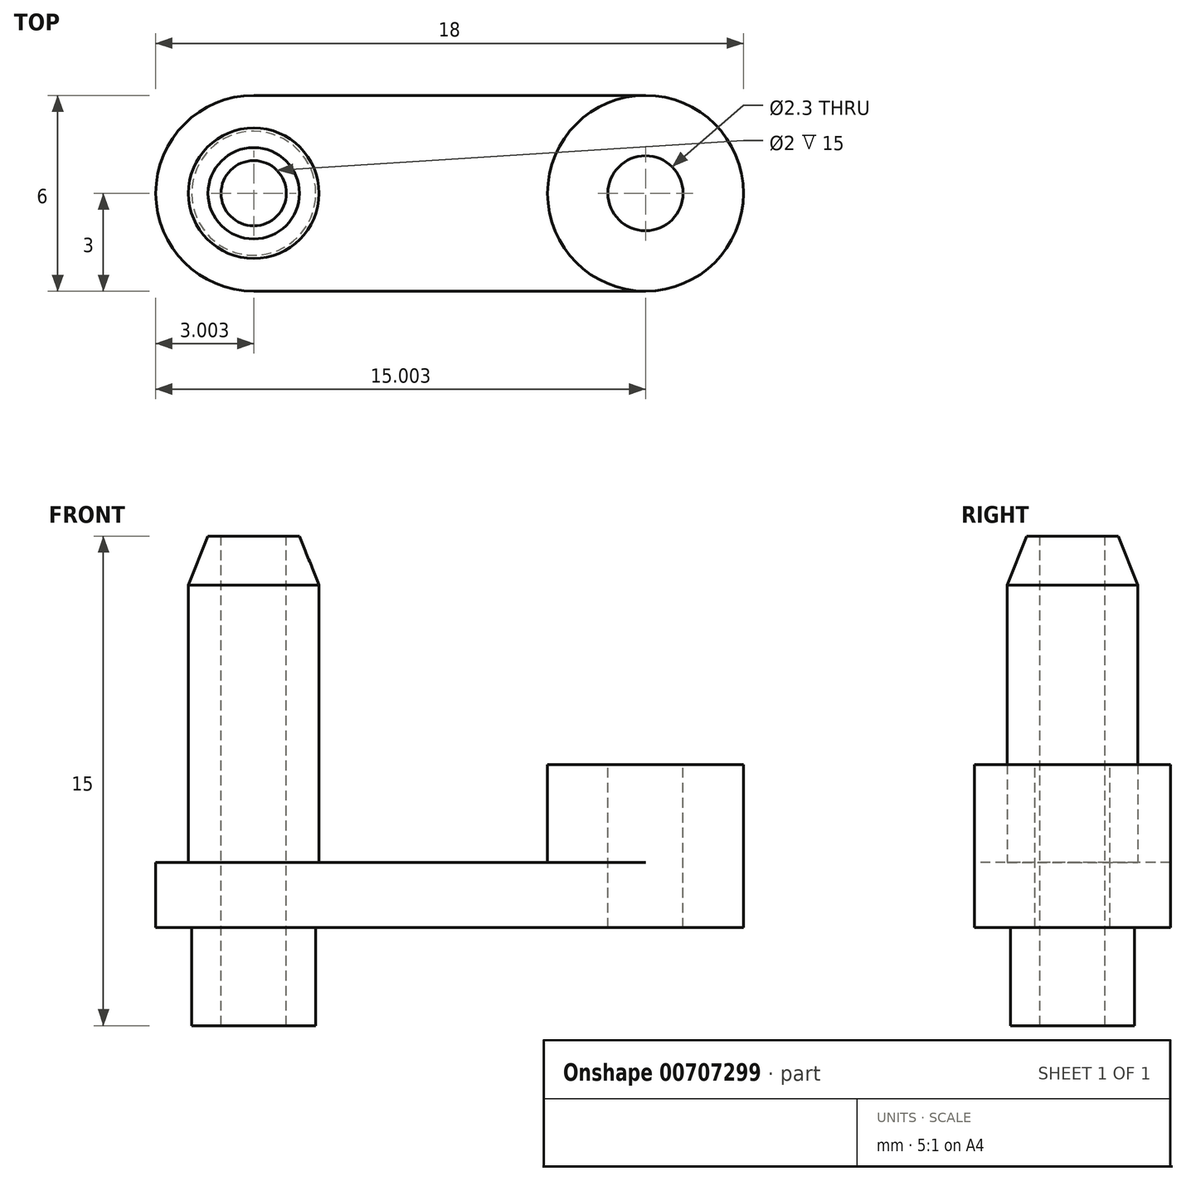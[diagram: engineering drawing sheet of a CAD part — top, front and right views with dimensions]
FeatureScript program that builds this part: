
annotation { "Feature Type Name" : "Feature", "Feature Type Description" : "" }
export const myFeature = defineFeature(function(context is Context, id is Id, definition is map)
    precondition{}
    {
        {
            var Q0;
            Q0=qCreatedBy(makeId("Top.planeOp"),FACE);
            var sketch = newSketch(context, id + "F0", { "sketchPlane" : qUnion([Q0])});
            skLineSegment(sketch, "E0.bottom", {"start": v(-7.1, 3) * mm, "end": v(10.9, 3) * mm});
            skLineSegment(sketch, "E0.top", {"start": v(-7.1, -3) * mm, "end": v(10.9, -3) * mm});
            skLineSegment(sketch, "E0.left", {"start": v(-7.1, 3) * mm, "end": v(-7.1, -3) * mm});
            skLineSegment(sketch, "E0.right", {"start": v(10.9, 3) * mm, "end": v(10.9, -3) * mm});
            skSolve(sketch);
        }
        {
            var Q0;
            Q0 = qSketchRegion(id + "F0", true);
            extrude(context, id + "F1", {"entities" : qUnion([Q0]), "depth" : 2 * mm, "offsetDistance" : 25 * mm});
        }
        {
            var Q0;
            Q0=makeQuery(id+"F1.opExtrude","CAP_FACE",FACE,{"disambiguationData":[OSD([sQuery(id+"F0.wireOp",EDGE,"E0.bottom"),sQuery(id+"F0.wireOp",EDGE,"E0.top"),sQuery(id+"F0.wireOp",EDGE,"E0.left"),sQuery(id+"F0.wireOp",EDGE,"E0.right")])],"isStart":false});
            var sketch = newSketch(context, id + "F2", { "sketchPlane" : qUnion([Q0])});
            skCircle(sketch, "E1", {"center": v(7.9, 0) * mm, "radius": 3 * mm});
            skCircle(sketch, "E2", {"center": v(-4.1, 0) * mm, "radius": 2 * mm});
            skSolve(sketch);
        }
        {
            var Q0;
            Q0 = qSketchRegion(id + "F2", true);
            extrude(context, id + "F3", {"entities" : qUnion([Q0]), "operationType" : NewBodyOperationType.ADD, "depth" : 10 * mm, "offsetDistance" : 25 * mm});
        }
        {
            var Q0;
            Q0=makeQuery(id+"F3.opExtrude","CAP_FACE",FACE,{"disambiguationData":[OSD([sQuery(id+"F2.wireOp",EDGE,"E2")])],"isStart":false});
            var sketch = newSketch(context, id + "F4", { "sketchPlane" : qUnion([Q0])});
            skCircle(sketch, "E3", {"center": v(-4.1, 0) * mm, "radius": 1 * mm});
            skCircle(sketch, "E4", {"center": v(7.9, 0) * mm, "radius": 1.15 * mm});
            skSolve(sketch);
        }
        {
            var Q0;
            Q0 = qSketchRegion(id + "F4", true);
            extrude(context, id + "F5", {"entities" : qUnion([Q0]), "operationType" : NewBodyOperationType.REMOVE, "oppositeDirection" : true, "depth" : 20 * mm, "offsetDistance" : 25 * mm});
        }
        {
            var Q0;
            Q0=makeQuery(id+"F3.opExtrude","CAP_EDGE",EDGE,{"disambiguationData":[OSD([sQuery(id+"F2.wireOp",EDGE,"E2")])],"isStart":false});
            chamfer(context, id + "F6", {"entities" : qUnion([Q0]), "chamferType" : ChamferType.TWO_OFFSETS, "width1" : 0.6 * mm, "oppositeDirection" : false, "width2" : 1.5 * mm, "tangentPropagation" : true});
        }
        {
            var Q0;
            Q0=makeQuery(id+"F3.opExtrude","CAP_FACE",FACE,{"disambiguationData":[OSD([sQuery(id+"F2.wireOp",EDGE,"E1")])],"isStart":false});
            var sketch = newSketch(context, id + "F7", { "sketchPlane" : qUnion([Q0])});
            skLineSegment(sketch, "E5.bottom", {"start": v(1.79, 5.38) * mm, "end": v(13.39, 5.38) * mm});
            skLineSegment(sketch, "E5.top", {"start": v(1.79, -6.45) * mm, "end": v(13.39, -6.45) * mm});
            skLineSegment(sketch, "E5.left", {"start": v(1.79, 5.38) * mm, "end": v(1.79, -6.45) * mm});
            skLineSegment(sketch, "E5.right", {"start": v(13.39, 5.38) * mm, "end": v(13.39, -6.45) * mm});
            skSolve(sketch);
        }
        {
            var Q0;
            Q0 = qSketchRegion(id + "F7", true);
            extrude(context, id + "F8", {"entities" : qUnion([Q0]), "operationType" : NewBodyOperationType.REMOVE, "oppositeDirection" : true, "depth" : 7 * mm, "offsetDistance" : 25 * mm});
        }
        {
            var Q0;
            Q0=makeQuery(id+"F1.opExtrude","SWEPT_EDGE",EDGE,{"disambiguationData":[OSD([sQuery(id+"F0.wireOp",EDGE,"E0.top"),sQuery(id+"F0.wireOp",EDGE,"E0.right")])]});
            var Q1;
            Q1=makeQuery(id+"F1.opExtrude","SWEPT_EDGE",EDGE,{"disambiguationData":[OSD([sQuery(id+"F0.wireOp",EDGE,"E0.bottom"),sQuery(id+"F0.wireOp",EDGE,"E0.right")])]});
            var Q2;
            Q2=makeQuery(id+"F1.opExtrude","SWEPT_EDGE",EDGE,{"disambiguationData":[OSD([sQuery(id+"F0.wireOp",EDGE,"E0.bottom"),sQuery(id+"F0.wireOp",EDGE,"E0.left")])]});
            var Q3;
            Q3=makeQuery(id+"F1.opExtrude","SWEPT_EDGE",EDGE,{"disambiguationData":[OSD([sQuery(id+"F0.wireOp",EDGE,"E0.top"),sQuery(id+"F0.wireOp",EDGE,"E0.left")])]});
            fillet(context, id + "F9", {"entities" : qUnion([Q0, Q1, Q2, Q3]), "radius" : 3 * mm, "tangentPropagation" : true, "allowEdgeOverflow" : false});
        }
        {
            var Q0;
            Q0=makeQuery(id+"F1.opExtrude","CAP_FACE",FACE,{"disambiguationData":[OSD([sQuery(id+"F0.wireOp",EDGE,"E0.bottom"),sQuery(id+"F0.wireOp",EDGE,"E0.top"),sQuery(id+"F0.wireOp",EDGE,"E0.left"),sQuery(id+"F0.wireOp",EDGE,"E0.right")])],"isStart":true});
            var sketch = newSketch(context, id + "F10", { "sketchPlane" : qUnion([Q0])});
            skCircle(sketch, "E6", {"center": v(-4.1, 0) * mm, "radius": 1.9 * mm});
            skCircle(sketch, "E7", {"center": v(-4.1, 0) * mm, "radius": 1 * mm});
            skSolve(sketch);
        }
        {
            var Q0;
            Q0 = qSketchRegion(id + "F10", true);
            extrude(context, id + "F11", {"entities" : qUnion([Q0]), "operationType" : NewBodyOperationType.ADD, "depth" : 3 * mm, "offsetDistance" : 25 * mm});
        }
    });
